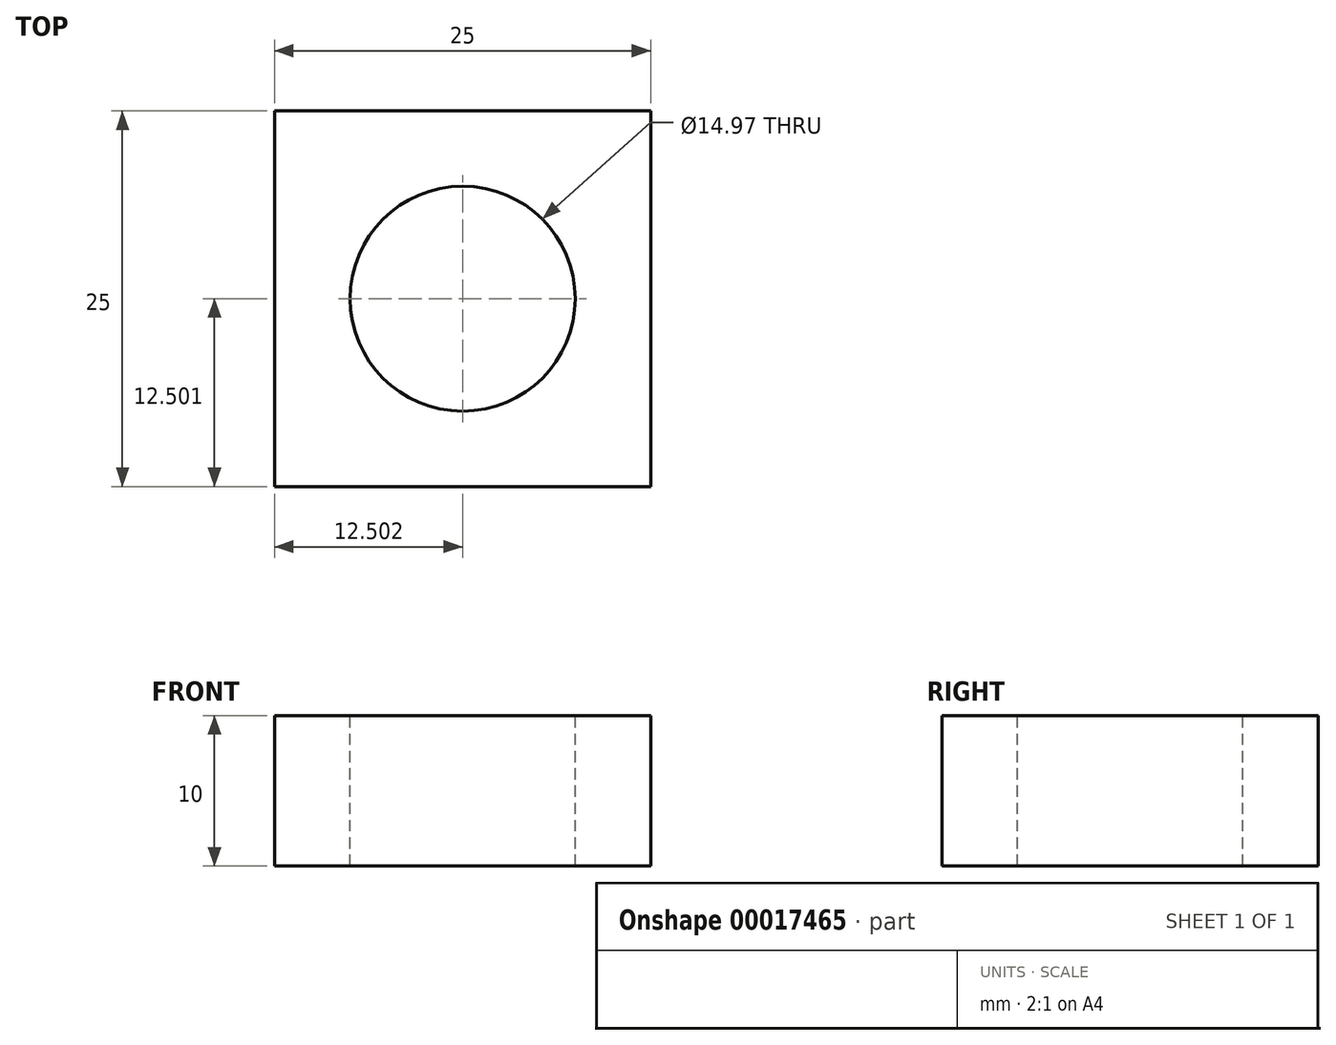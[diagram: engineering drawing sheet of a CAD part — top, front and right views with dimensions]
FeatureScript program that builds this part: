
annotation { "Feature Type Name" : "Feature", "Feature Type Description" : "" }
export const myFeature = defineFeature(function(context is Context, id is Id, definition is map)
    precondition{}
    {
        {
            var Q0;
            Q0=qCreatedBy(makeId("Top.planeOp"),FACE);
            var sketch = newSketch(context, id + "F0", { "sketchPlane" : qUnion([Q0])});
            skLineSegment(sketch, "E0", {"start": v(-14.19, 10.2) * mm, "end": v(-14.19, -14.8) * mm});
            skLineSegment(sketch, "E1", {"start": v(-14.19, -14.8) * mm, "end": v(10.81, -14.8) * mm});
            skLineSegment(sketch, "E2", {"start": v(10.81, -14.8) * mm, "end": v(10.81, 10.2) * mm});
            skLineSegment(sketch, "E3", {"start": v(10.81, 10.2) * mm, "end": v(-14.19, 10.2) * mm});
            skSolve(sketch);
        }
        {
            var Q0;
            Q0=makeQuery(id+"F0.imprint","IMPRINT",FACE,{"disambiguationData":[TD([[makeQuery(id+"F0.imprint","IMPRINT",EDGE,{"derivedFrom":sQuery(id+"F0.wireOp",EDGE,"E0")}),1.0]])]});
            extrude(context, id + "F1", {"entities" : qUnion([Q0]), "oppositeDirection" : true, "depth" : 10 * mm});
        }
        {
            var Q0;
            Q0=makeQuery(id+"F1.opExtrude","CAP_FACE",FACE,{"disambiguationData":[OSD([sQuery(id+"F0.wireOp",EDGE,"E0"),sQuery(id+"F0.wireOp",EDGE,"E1"),sQuery(id+"F0.wireOp",EDGE,"E2"),sQuery(id+"F0.wireOp",EDGE,"E3")])],"isStart":true});
            var sketch = newSketch(context, id + "F2", { "sketchPlane" : qUnion([Q0])});
            skLineSegment(sketch, "E4", {"start": v(10.81, -14.8) * mm, "end": v(10.81, 10.2) * mm});
            skLineSegment(sketch, "E5", {"start": v(-14.19, -14.8) * mm, "end": v(-14.19, 10.2) * mm});
            skCircle(sketch, "E6", {"center": v(-1.69, -2.3) * mm, "radius": 7.48 * mm});
            skSolve(sketch);
        }
        {
            var Q0;
            Q0=makeQuery(id+"F2.imprint","IMPRINT",FACE,{"disambiguationData":[TD([[makeQuery(id+"F2.imprint","IMPRINT",EDGE,{"derivedFrom":sQuery(id+"F2.wireOp",EDGE,"E6")}),1.0]])]});
            var Q1;
            Q1=sQuery(id+"F2.wireOp",EDGE,"E6");
            extrude(context, id + "F3", {"entities" : qUnion([Q0]), "operationType" : NewBodyOperationType.REMOVE, "surfaceEntities" : qUnion([Q1]), "oppositeDirection" : true, "depth" : 25 * mm});
        }
    });
